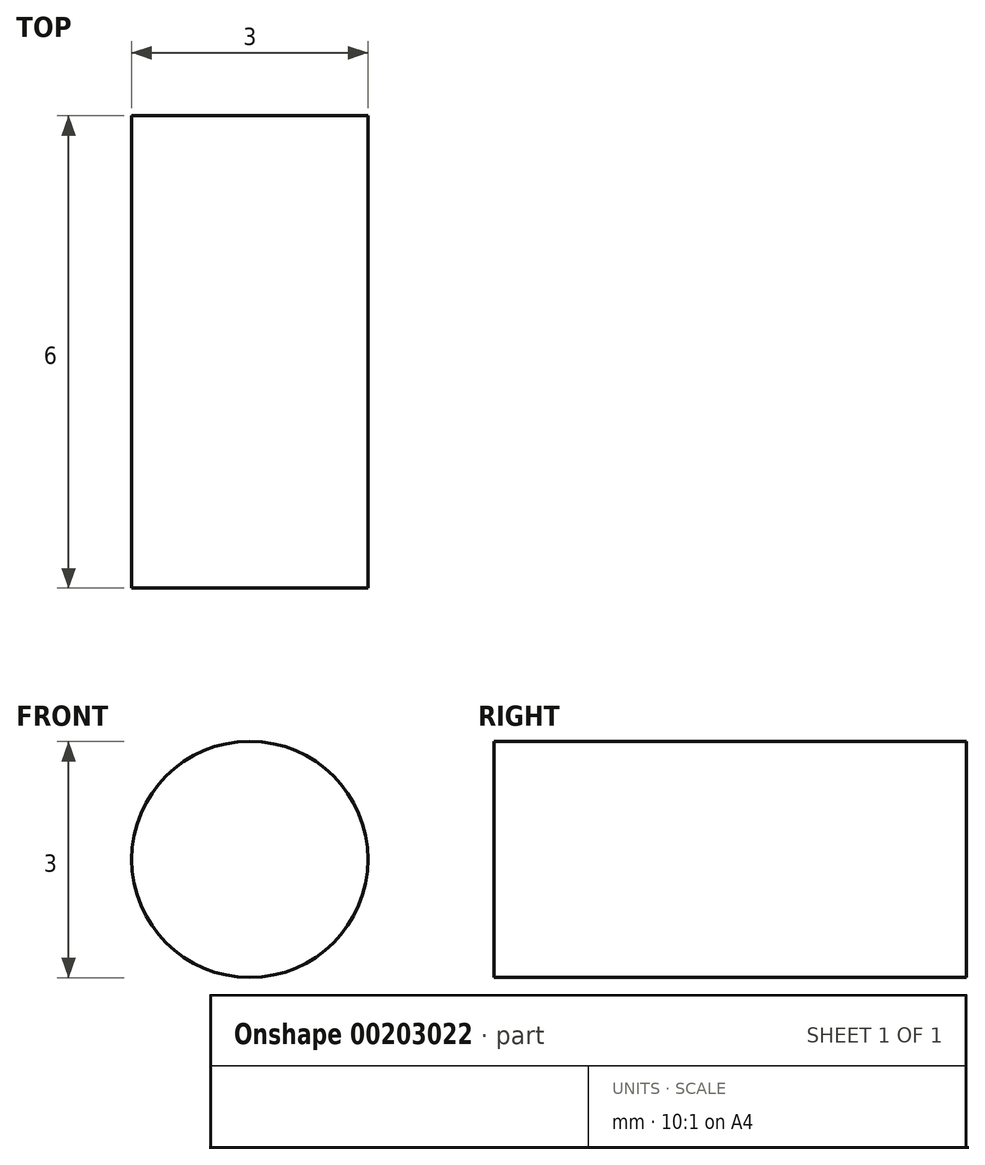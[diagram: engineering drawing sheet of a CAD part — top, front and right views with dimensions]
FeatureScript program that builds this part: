
annotation { "Feature Type Name" : "Feature", "Feature Type Description" : "" }
export const myFeature = defineFeature(function(context is Context, id is Id, definition is map)
    precondition{}
    {
        {
            var Q0;
            Q0=qCreatedBy(makeId("Front.planeOp"),FACE);
            var sketch = newSketch(context, id + "F0", { "sketchPlane" : qUnion([Q0])});
            skCircle(sketch, "E0", {"center": v(50, -33) * mm, "radius": 1.5 * mm});
            skCircle(sketch, "E1", {"center": v(50, 46.6) * mm, "radius": 1.5 * mm});
            skCircle(sketch, "E2", {"center": v(-50, -33) * mm, "radius": 1.5 * mm});
            skCircle(sketch, "E3", {"center": v(-50, 46.6) * mm, "radius": 1.5 * mm});
            skLineSegment(sketch, "E4", {"start": v(-47, -39.5) * mm, "end": v(-47, -36.5) * mm});
            skLineSegment(sketch, "E5", {"start": v(-47, -36.5) * mm, "end": v(-53, -36.5) * mm});
            skLineSegment(sketch, "E6", {"start": v(-53, -36.5) * mm, "end": v(-53, -39.5) * mm});
            skLineSegment(sketch, "E7", {"start": v(-53, -39.5) * mm, "end": v(-47, -39.5) * mm});
            skLineSegment(sketch, "E8", {"start": v(-47, -26.5) * mm, "end": v(-47, -29.5) * mm});
            skLineSegment(sketch, "E9", {"start": v(-47, -29.5) * mm, "end": v(-53, -29.5) * mm});
            skLineSegment(sketch, "E10", {"start": v(-53, -29.5) * mm, "end": v(-53, -26.5) * mm});
            skLineSegment(sketch, "E11", {"start": v(-53, -26.5) * mm, "end": v(-47, -26.5) * mm});
            skLineSegment(sketch, "E12", {"start": v(-53, 40.1) * mm, "end": v(-53, 43.1) * mm});
            skLineSegment(sketch, "E13", {"start": v(-53, 43.1) * mm, "end": v(-47, 43.1) * mm});
            skLineSegment(sketch, "E14", {"start": v(-47, 43.1) * mm, "end": v(-47, 40.1) * mm});
            skLineSegment(sketch, "E15", {"start": v(-47, 40.1) * mm, "end": v(-53, 40.1) * mm});
            skLineSegment(sketch, "E16", {"start": v(-53, 53.1) * mm, "end": v(-53, 50.1) * mm});
            skLineSegment(sketch, "E17", {"start": v(-53, 50.1) * mm, "end": v(-47, 50.1) * mm});
            skLineSegment(sketch, "E18", {"start": v(-47, 50.1) * mm, "end": v(-47, 53.1) * mm});
            skLineSegment(sketch, "E19", {"start": v(-47, 53.1) * mm, "end": v(-53, 53.1) * mm});
            skLineSegment(sketch, "E20", {"start": v(53, 40.1) * mm, "end": v(53, 43.1) * mm});
            skLineSegment(sketch, "E21", {"start": v(53, 43.1) * mm, "end": v(47, 43.1) * mm});
            skLineSegment(sketch, "E22", {"start": v(47, 43.1) * mm, "end": v(47, 40.1) * mm});
            skLineSegment(sketch, "E23", {"start": v(47, 40.1) * mm, "end": v(53, 40.1) * mm});
            skLineSegment(sketch, "E24", {"start": v(53, 53.1) * mm, "end": v(53, 50.1) * mm});
            skLineSegment(sketch, "E25", {"start": v(53, 50.1) * mm, "end": v(47, 50.1) * mm});
            skLineSegment(sketch, "E26", {"start": v(47, 50.1) * mm, "end": v(47, 53.1) * mm});
            skLineSegment(sketch, "E27", {"start": v(47, 53.1) * mm, "end": v(53, 53.1) * mm});
            skLineSegment(sketch, "E28", {"start": v(47, -39.5) * mm, "end": v(47, -36.5) * mm});
            skLineSegment(sketch, "E29", {"start": v(47, -36.5) * mm, "end": v(53, -36.5) * mm});
            skLineSegment(sketch, "E30", {"start": v(53, -36.5) * mm, "end": v(53, -39.5) * mm});
            skLineSegment(sketch, "E31", {"start": v(53, -39.5) * mm, "end": v(47, -39.5) * mm});
            skLineSegment(sketch, "E32", {"start": v(47, -26.5) * mm, "end": v(47, -29.5) * mm});
            skLineSegment(sketch, "E33", {"start": v(47, -29.5) * mm, "end": v(53, -29.5) * mm});
            skLineSegment(sketch, "E34", {"start": v(53, -29.5) * mm, "end": v(53, -26.5) * mm});
            skLineSegment(sketch, "E35", {"start": v(53, -26.5) * mm, "end": v(47, -26.5) * mm});
            skLineSegment(sketch, "E36", {"start": v(14.9, -29.8) * mm, "end": v(14.9, -46.3) * mm});
            skLineSegment(sketch, "E37", {"start": v(14.9, -46.3) * mm, "end": v(20.3, -46.3) * mm});
            skLineSegment(sketch, "E38", {"start": v(20.3, -46.3) * mm, "end": v(20.3, -29.8) * mm});
            skLineSegment(sketch, "E39", {"start": v(20.3, -9.7) * mm, "end": v(20.3, 6.8) * mm});
            skLineSegment(sketch, "E40", {"start": v(14.9, 6.8) * mm, "end": v(14.9, -9.7) * mm});
            skLineSegment(sketch, "E41", {"start": v(-14.9, -29.8) * mm, "end": v(-14.9, -46.3) * mm});
            skLineSegment(sketch, "E42", {"start": v(-14.9, -46.3) * mm, "end": v(-20.3, -46.3) * mm});
            skLineSegment(sketch, "E43", {"start": v(-20.3, -46.3) * mm, "end": v(-20.3, -29.8) * mm});
            skLineSegment(sketch, "E44", {"start": v(-20.3, -9.7) * mm, "end": v(-20.3, 6.8) * mm});
            skLineSegment(sketch, "E45", {"start": v(-14.9, 6.8) * mm, "end": v(-14.9, -9.7) * mm});
            skLineSegment(sketch, "E46", {"start": v(23, 41.6) * mm, "end": v(23, 44.6) * mm});
            skLineSegment(sketch, "E47", {"start": v(23, 44.6) * mm, "end": v(17, 44.6) * mm});
            skLineSegment(sketch, "E48", {"start": v(17, 44.6) * mm, "end": v(17, 41.6) * mm});
            skLineSegment(sketch, "E49", {"start": v(17, 41.6) * mm, "end": v(23, 41.6) * mm});
            skLineSegment(sketch, "E50", {"start": v(-23, 41.6) * mm, "end": v(-23, 44.6) * mm});
            skLineSegment(sketch, "E51", {"start": v(-23, 44.6) * mm, "end": v(-17, 44.6) * mm});
            skLineSegment(sketch, "E52", {"start": v(30.98, -40.02) * mm, "end": v(25.29, -41.92) * mm});
            skLineSegment(sketch, "E53", {"start": v(25.29, -41.92) * mm, "end": v(24.34, -39.07) * mm});
            skLineSegment(sketch, "E54", {"start": v(24.34, -39.07) * mm, "end": v(30.03, -37.18) * mm});
            skLineSegment(sketch, "E55", {"start": v(-3, -47) * mm, "end": v(-3, -50) * mm});
            skLineSegment(sketch, "E56", {"start": v(-3, -50) * mm, "end": v(3, -50) * mm});
            skLineSegment(sketch, "E57", {"start": v(3, -50) * mm, "end": v(3, -47) * mm});
            skLineSegment(sketch, "E58", {"start": v(3, -47) * mm, "end": v(-3, -47) * mm});
            skLineSegment(sketch, "E59", {"start": v(14.9, -15.1) * mm, "end": v(3, -15.1) * mm});
            skLineSegment(sketch, "E60", {"start": v(-3, -9.7) * mm, "end": v(-3, -15.1) * mm});
            skLineSegment(sketch, "E61", {"start": v(14.9, 6.8) * mm, "end": v(20.3, 6.8) * mm});
            skLineSegment(sketch, "E62", {"start": v(-20.3, 6.8) * mm, "end": v(-14.9, 6.8) * mm});
            skLineSegment(sketch, "E63", {"start": v(-20.3, -24.4) * mm, "end": v(-26.9, -24.4) * mm});
            skLineSegment(sketch, "E64", {"start": v(-26.9, -24.4) * mm, "end": v(-26.9, -29.8) * mm});
            skLineSegment(sketch, "E65", {"start": v(-26.9, -29.8) * mm, "end": v(-20.3, -29.8) * mm});
            skLineSegment(sketch, "E66", {"start": v(-20.3, -9.7) * mm, "end": v(-26.9, -9.7) * mm});
            skLineSegment(sketch, "E67", {"start": v(-26.9, -9.7) * mm, "end": v(-26.9, -15.1) * mm});
            skLineSegment(sketch, "E68", {"start": v(-26.9, -15.1) * mm, "end": v(-20.3, -15.1) * mm});
            skLineSegment(sketch, "E69", {"start": v(-20.3, -24.4) * mm, "end": v(-20.3, -15.1) * mm});
            skLineSegment(sketch, "E70", {"start": v(-3, -24.4) * mm, "end": v(-3, -29.8) * mm});
            skLineSegment(sketch, "E71", {"start": v(-14.9, -29.8) * mm, "end": v(-3, -29.8) * mm});
            skLineSegment(sketch, "E72", {"start": v(-3, -24.4) * mm, "end": v(-14.9, -24.4) * mm});
            skLineSegment(sketch, "E73", {"start": v(-14.9, -15.1) * mm, "end": v(-3, -15.1) * mm});
            skLineSegment(sketch, "E74", {"start": v(-3, -9.7) * mm, "end": v(-14.9, -9.7) * mm});
            skLineSegment(sketch, "E75", {"start": v(-14.9, -24.4) * mm, "end": v(-14.9, -15.1) * mm});
            skLineSegment(sketch, "E76", {"start": v(20.3, -24.4) * mm, "end": v(26.9, -24.4) * mm});
            skLineSegment(sketch, "E77", {"start": v(26.9, -24.4) * mm, "end": v(26.9, -29.8) * mm});
            skLineSegment(sketch, "E78", {"start": v(26.9, -29.8) * mm, "end": v(20.3, -29.8) * mm});
            skLineSegment(sketch, "E79", {"start": v(20.3, -9.7) * mm, "end": v(26.9, -9.7) * mm});
            skLineSegment(sketch, "E80", {"start": v(26.9, -9.7) * mm, "end": v(26.9, -15.1) * mm});
            skLineSegment(sketch, "E81", {"start": v(26.9, -15.1) * mm, "end": v(20.3, -15.1) * mm});
            skLineSegment(sketch, "E82", {"start": v(20.3, -24.4) * mm, "end": v(20.3, -15.1) * mm});
            skLineSegment(sketch, "E83", {"start": v(14.9, -24.4) * mm, "end": v(14.9, -15.1) * mm});
            skLineSegment(sketch, "E84", {"start": v(3, -9.7) * mm, "end": v(14.9, -9.7) * mm});
            skLineSegment(sketch, "E85", {"start": v(3, -9.7) * mm, "end": v(3, -15.1) * mm});
            skLineSegment(sketch, "E86", {"start": v(3, -24.4) * mm, "end": v(3, -29.8) * mm});
            skLineSegment(sketch, "E87", {"start": v(14.9, -29.8) * mm, "end": v(3, -29.8) * mm});
            skLineSegment(sketch, "E88", {"start": v(3, -24.4) * mm, "end": v(14.9, -24.4) * mm});
            skLineSegment(sketch, "E89", {"start": v(23, 55.6) * mm, "end": v(23, 50.6) * mm});
            skLineSegment(sketch, "E90", {"start": v(23, 50.6) * mm, "end": v(20, 50.6) * mm});
            skLineSegment(sketch, "E91", {"start": v(20, 50.6) * mm, "end": v(17, 50.6) * mm});
            skLineSegment(sketch, "E92", {"start": v(17, 50.6) * mm, "end": v(17, 55.6) * mm});
            skLineSegment(sketch, "E93", {"start": v(17, 55.6) * mm, "end": v(16, 56.6) * mm});
            skLineSegment(sketch, "E94", {"start": v(16, 56.6) * mm, "end": v(-16, 56.6) * mm});
            skLineSegment(sketch, "E95", {"start": v(-16, 56.6) * mm, "end": v(-17, 55.6) * mm});
            skLineSegment(sketch, "E96", {"start": v(-17, 55.6) * mm, "end": v(-17, 50.6) * mm});
            skLineSegment(sketch, "E97", {"start": v(-17, 50.6) * mm, "end": v(-20, 50.6) * mm});
            skLineSegment(sketch, "E98", {"start": v(-20, 50.6) * mm, "end": v(-23, 50.6) * mm});
            skLineSegment(sketch, "E99", {"start": v(-23, 50.6) * mm, "end": v(-23, 55.6) * mm});
            skLineSegment(sketch, "E100", {"start": v(-23, 55.6) * mm, "end": v(-24, 56.6) * mm});
            skLineSegment(sketch, "E101", {"start": v(-24, 56.6) * mm, "end": v(-55, 56.6) * mm});
            skArc(sketch, "E102", {"start": v(-55, 56.6) * mm, "mid": v(-58.54, 55.15) * mm, "end": v(-60, 51.6) * mm});
            skLineSegment(sketch, "E103", {"start": v(-60, 51.6) * mm, "end": v(-60, -39.4) * mm});
            skArc(sketch, "E104", {"start": v(-60, -39.4) * mm, "mid": v(-59.06, -42.32) * mm, "end": v(-56.58, -44.14) * mm});
            skLineSegment(sketch, "E105", {"start": v(-56.58, -44.14) * mm, "end": v(-35.72, -51.09) * mm});
            skLineSegment(sketch, "E106", {"start": v(-35.72, -51.09) * mm, "end": v(-34.46, -50.46) * mm});
            skLineSegment(sketch, "E107", {"start": v(-34.46, -50.46) * mm, "end": v(-32.88, -45.71) * mm});
            skLineSegment(sketch, "E108", {"start": v(-32.88, -45.71) * mm, "end": v(-30.03, -46.66) * mm});
            skLineSegment(sketch, "E109", {"start": v(-30.03, -46.66) * mm, "end": v(-27.18, -47.61) * mm});
            skLineSegment(sketch, "E110", {"start": v(-27.18, -47.61) * mm, "end": v(-28.76, -52.35) * mm});
            skLineSegment(sketch, "E111", {"start": v(-28.76, -52.35) * mm, "end": v(-28.13, -53.62) * mm});
            skLineSegment(sketch, "E112", {"start": v(-28.13, -53.62) * mm, "end": v(-4.32, -61.56) * mm});
            skArc(sketch, "E113", {"start": v(-4.32, -61.56) * mm, "mid": v(-3.42, -61.42) * mm, "end": v(-3, -60.6) * mm});
            skLineSegment(sketch, "E114", {"start": v(-3, -60.6) * mm, "end": v(-3, -56) * mm});
            skLineSegment(sketch, "E115", {"start": v(-3, -56) * mm, "end": v(0, -56) * mm});
            skLineSegment(sketch, "E116", {"start": v(0, -56) * mm, "end": v(3, -56) * mm});
            skLineSegment(sketch, "E117", {"start": v(3, -56) * mm, "end": v(3, -60.6) * mm});
            skArc(sketch, "E118", {"start": v(3, -60.6) * mm, "mid": v(3.42, -61.42) * mm, "end": v(4.32, -61.56) * mm});
            skLineSegment(sketch, "E119", {"start": v(4.32, -61.56) * mm, "end": v(28.13, -53.62) * mm});
            skLineSegment(sketch, "E120", {"start": v(28.13, -53.62) * mm, "end": v(28.76, -52.35) * mm});
            skLineSegment(sketch, "E121", {"start": v(28.76, -52.35) * mm, "end": v(27.18, -47.61) * mm});
            skLineSegment(sketch, "E122", {"start": v(27.18, -47.61) * mm, "end": v(30.03, -46.66) * mm});
            skLineSegment(sketch, "E123", {"start": v(30.03, -46.66) * mm, "end": v(32.88, -45.71) * mm});
            skLineSegment(sketch, "E124", {"start": v(32.88, -45.71) * mm, "end": v(34.46, -50.46) * mm});
            skLineSegment(sketch, "E125", {"start": v(34.46, -50.46) * mm, "end": v(35.72, -51.09) * mm});
            skLineSegment(sketch, "E126", {"start": v(35.72, -51.09) * mm, "end": v(56.58, -44.14) * mm});
            skArc(sketch, "E127", {"start": v(56.58, -44.14) * mm, "mid": v(59.06, -42.32) * mm, "end": v(60, -39.4) * mm});
            skLineSegment(sketch, "E128", {"start": v(60, -39.4) * mm, "end": v(60, 51.6) * mm});
            skArc(sketch, "E129", {"start": v(60, 51.6) * mm, "mid": v(58.54, 55.15) * mm, "end": v(55, 56.6) * mm});
            skLineSegment(sketch, "E130", {"start": v(55, 56.6) * mm, "end": v(24, 56.6) * mm});
            skLineSegment(sketch, "E131", {"start": v(24, 56.6) * mm, "end": v(23, 55.6) * mm});
            skLineSegment(sketch, "E132", {"start": v(-28.72, 24.9) * mm, "end": v(-28.72, 30.9) * mm});
            skLineSegment(sketch, "E133", {"start": v(-28.72, 30.9) * mm, "end": v(-22.72, 30.9) * mm});
            skLineSegment(sketch, "E134", {"start": v(-22.72, 30.9) * mm, "end": v(-22.72, 24.9) * mm});
            skLineSegment(sketch, "E135", {"start": v(-22.72, 24.9) * mm, "end": v(-28.72, 24.9) * mm});
            skLineSegment(sketch, "E136", {"start": v(28.72, 24.9) * mm, "end": v(28.72, 30.9) * mm});
            skLineSegment(sketch, "E137", {"start": v(28.72, 30.9) * mm, "end": v(22.72, 30.9) * mm});
            skLineSegment(sketch, "E138", {"start": v(22.72, 30.9) * mm, "end": v(22.72, 24.9) * mm});
            skLineSegment(sketch, "E139", {"start": v(22.72, 24.9) * mm, "end": v(28.72, 24.9) * mm});
            skLineSegment(sketch, "E140", {"start": v(28.72, 9.9) * mm, "end": v(28.72, 15.9) * mm});
            skLineSegment(sketch, "E141", {"start": v(28.72, 15.9) * mm, "end": v(22.72, 15.9) * mm});
            skLineSegment(sketch, "E142", {"start": v(22.72, 15.9) * mm, "end": v(22.72, 9.9) * mm});
            skLineSegment(sketch, "E143", {"start": v(22.72, 9.9) * mm, "end": v(28.72, 9.9) * mm});
            skLineSegment(sketch, "E144", {"start": v(-28.72, 9.9) * mm, "end": v(-28.72, 15.9) * mm});
            skLineSegment(sketch, "E145", {"start": v(-28.72, 15.9) * mm, "end": v(-22.72, 15.9) * mm});
            skLineSegment(sketch, "E146", {"start": v(-22.72, 15.9) * mm, "end": v(-22.72, 9.9) * mm});
            skLineSegment(sketch, "E147", {"start": v(-22.72, 9.9) * mm, "end": v(-28.72, 9.9) * mm});
            skCircle(sketch, "E148", {"center": v(-40, -23) * mm, "radius": 1.6 * mm});
            skCircle(sketch, "E149", {"center": v(40, -23) * mm, "radius": 1.6 * mm});
            skCircle(sketch, "E150", {"center": v(-40, -13) * mm, "radius": 1.6 * mm});
            skCircle(sketch, "E151", {"center": v(40, -13) * mm, "radius": 1.6 * mm});
            skCircle(sketch, "E152", {"center": v(-40, -3) * mm, "radius": 1.6 * mm});
            skCircle(sketch, "E153", {"center": v(-30, -3) * mm, "radius": 1.6 * mm});
            skCircle(sketch, "E154", {"center": v(0, -3) * mm, "radius": 1.6 * mm});
            skCircle(sketch, "E155", {"center": v(30, -3) * mm, "radius": 1.6 * mm});
            skCircle(sketch, "E156", {"center": v(40, -3) * mm, "radius": 1.6 * mm});
            skCircle(sketch, "E157", {"center": v(-40, 7) * mm, "radius": 1.6 * mm});
            skCircle(sketch, "E158", {"center": v(0, 7) * mm, "radius": 1.6 * mm});
            skCircle(sketch, "E159", {"center": v(40, 7) * mm, "radius": 1.6 * mm});
            skCircle(sketch, "E160", {"center": v(-40, 17) * mm, "radius": 1.6 * mm});
            skCircle(sketch, "E161", {"center": v(-10, 17) * mm, "radius": 1.6 * mm});
            skCircle(sketch, "E162", {"center": v(0, 17) * mm, "radius": 1.6 * mm});
            skCircle(sketch, "E163", {"center": v(10, 17) * mm, "radius": 1.6 * mm});
            skCircle(sketch, "E164", {"center": v(40, 17) * mm, "radius": 1.6 * mm});
            skCircle(sketch, "E165", {"center": v(-40, 27) * mm, "radius": 1.6 * mm});
            skCircle(sketch, "E166", {"center": v(-20, 27) * mm, "radius": 1.6 * mm});
            skCircle(sketch, "E167", {"center": v(-10, 27) * mm, "radius": 1.6 * mm});
            skCircle(sketch, "E168", {"center": v(0, 27) * mm, "radius": 1.6 * mm});
            skCircle(sketch, "E169", {"center": v(10, 27) * mm, "radius": 1.6 * mm});
            skCircle(sketch, "E170", {"center": v(20, 27) * mm, "radius": 1.6 * mm});
            skCircle(sketch, "E171", {"center": v(40, 27) * mm, "radius": 1.6 * mm});
            skCircle(sketch, "E172", {"center": v(-40, 37) * mm, "radius": 1.6 * mm});
            skCircle(sketch, "E173", {"center": v(-30, 37) * mm, "radius": 1.6 * mm});
            skCircle(sketch, "E174", {"center": v(-20, 37) * mm, "radius": 1.6 * mm});
            skCircle(sketch, "E175", {"center": v(-10, 37) * mm, "radius": 1.6 * mm});
            skCircle(sketch, "E176", {"center": v(0, 37) * mm, "radius": 1.6 * mm});
            skCircle(sketch, "E177", {"center": v(10, 37) * mm, "radius": 1.6 * mm});
            skCircle(sketch, "E178", {"center": v(20, 37) * mm, "radius": 1.6 * mm});
            skCircle(sketch, "E179", {"center": v(30, 37) * mm, "radius": 1.6 * mm});
            skCircle(sketch, "E180", {"center": v(40, 37) * mm, "radius": 1.6 * mm});
            skLineSegment(sketch, "E181", {"start": v(30.03, -37.18) * mm, "end": v(30.98, -40.02) * mm});
            skLineSegment(sketch, "E182.MirrorCS", {"start": v(-30.98, -40.02) * mm, "end": v(-25.29, -41.92) * mm});
            skLineSegment(sketch, "E183.MirrorCS", {"start": v(-25.29, -41.92) * mm, "end": v(-24.34, -39.07) * mm});
            skLineSegment(sketch, "E184.MirrorCS", {"start": v(-30.03, -37.18) * mm, "end": v(-30.98, -40.02) * mm});
            skLineSegment(sketch, "E185.MirrorCS", {"start": v(-24.34, -39.07) * mm, "end": v(-30.03, -37.18) * mm});
            skLineSegment(sketch, "E186", {"start": v(-23, 41.6) * mm, "end": v(-17, 41.6) * mm});
            skLineSegment(sketch, "E187", {"start": v(-17, 41.6) * mm, "end": v(-17, 44.6) * mm});
            skSolve(sketch);
        }
        {
            var Q0;
            Q0=makeQuery(id+"F0.imprint","IMPRINT",FACE,{"disambiguationData":[TD([[makeQuery(id+"F0.imprint","IMPRINT",EDGE,{"derivedFrom":sQuery(id+"F0.wireOp",EDGE,"E0")}),1.0]])]});
            extrude(context, id + "F1", {"entities" : qUnion([Q0]), "depth" : 6 * mm});
        }
    });
